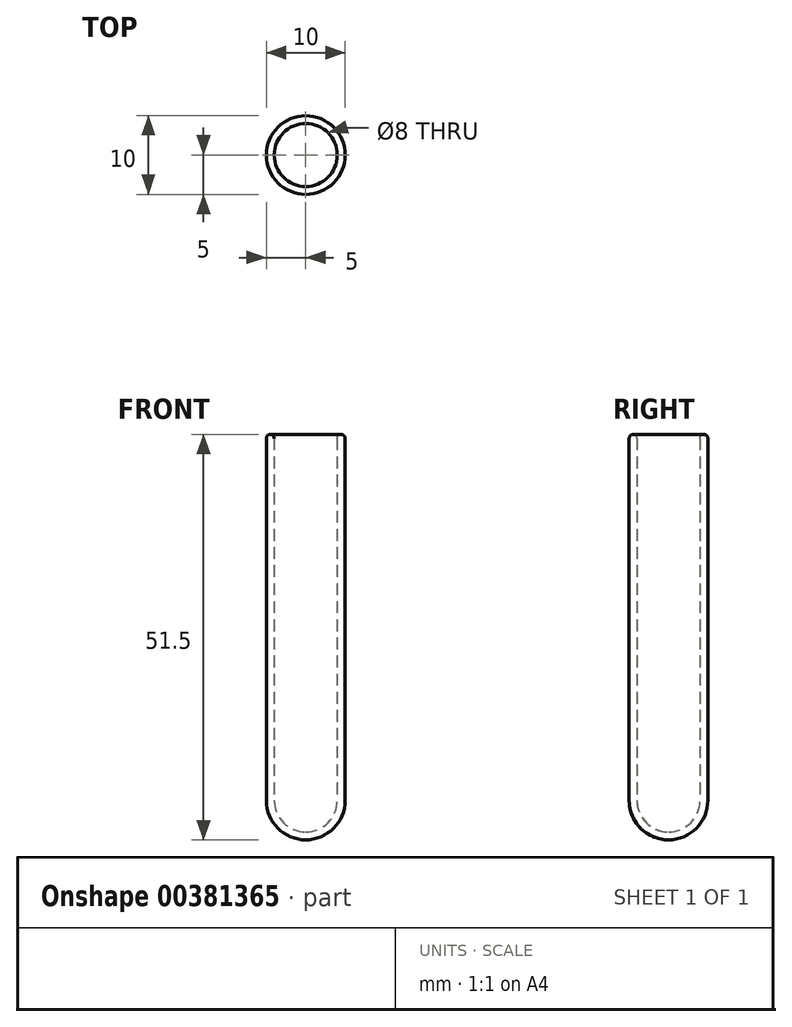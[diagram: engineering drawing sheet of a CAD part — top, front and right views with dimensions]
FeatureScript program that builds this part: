
annotation { "Feature Type Name" : "Feature", "Feature Type Description" : "" }
export const myFeature = defineFeature(function(context is Context, id is Id, definition is map)
    precondition{}
    {
        {
            var Q0;
            Q0=qCreatedBy(makeId("Right.planeOp"),FACE);
            var sketch = newSketch(context, id + "F0", { "sketchPlane" : qUnion([Q0])});
            skLineSegment(sketch, "E0", {"start": v(0, 0) * mm, "end": v(0, 42.16) * mm, "construction": true});
            skLineSegment(sketch, "E1", {"start": v(-4, 46) * mm, "end": v(-4, 0) * mm});
            skArc(sketch, "E2", {"start": v(-4, 0) * mm, "mid": v(-2.83, -2.83) * mm, "end": v(0, -4) * mm});
            skArc(sketch, "E3.0", {"start": v(-5, 0) * mm, "mid": v(-3.54, -3.54) * mm, "end": v(0, -5) * mm});
            skLineSegment(sketch, "E3.1", {"start": v(-5, 46) * mm, "end": v(-5, 0) * mm});
            skArc(sketch, "E4", {"start": v(-4, 46) * mm, "mid": v(-4.5, 46.5) * mm, "end": v(-5, 46) * mm});
            skLineSegment(sketch, "E5", {"start": v(0, -4) * mm, "end": v(0, -5) * mm});
            skSolve(sketch);
        }
        {
            var Q0;
            Q0=makeQuery(id+"F0.imprint","IMPRINT",FACE,{"disambiguationData":[TD([[makeQuery(id+"F0.imprint","IMPRINT",EDGE,{"derivedFrom":sQuery(id+"F0.wireOp",EDGE,"E1")}),-1.0]])]});
            var Q1;
            Q1=sQuery(id+"F0.wireOp",EDGE,"E0");
            revolve(context, id + "F1", {"entities" : qUnion([Q0]), "axis" : qUnion([Q1]), "revolveType" : RevolveType.FULL});
        }
    });
